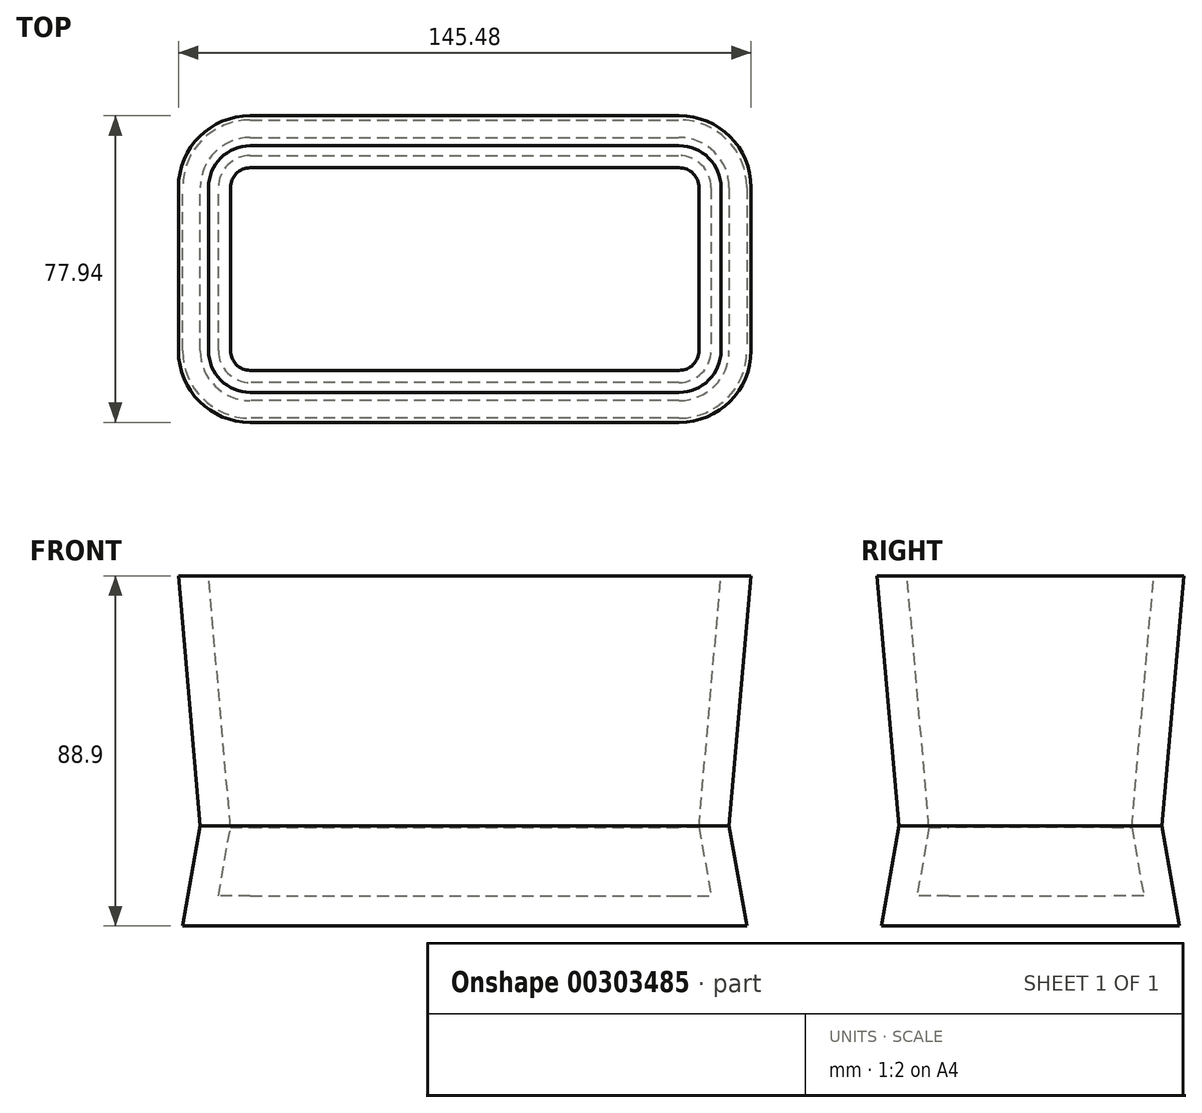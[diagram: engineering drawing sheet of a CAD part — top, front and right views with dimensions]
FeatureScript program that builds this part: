
annotation { "Feature Type Name" : "Feature", "Feature Type Description" : "" }
export const myFeature = defineFeature(function(context is Context, id is Id, definition is map)
    precondition{}
    {
        {
            var Q0;
            Q0=qCreatedBy(makeId("Top.planeOp"),FACE);
            var sketch = newSketch(context, id + "F0", { "sketchPlane" : qUnion([Q0])});
            skLineSegment(sketch, "E0.bottom", {"start": v(-54.48, 33.42) * mm, "end": v(54.48, 33.42) * mm});
            skLineSegment(sketch, "E0.top", {"start": v(-54.48, -33.42) * mm, "end": v(54.48, -33.42) * mm});
            skLineSegment(sketch, "E0.left", {"start": v(-67.18, 20.72) * mm, "end": v(-67.18, -20.72) * mm});
            skLineSegment(sketch, "E0.right", {"start": v(67.18, 20.72) * mm, "end": v(67.18, -20.72) * mm});
            skPoint(sketch, "E0.middle", {"position": v(0, 0) * mm});
            skPoint(sketch, "E1.visualSharp", {"position": v(-67.18, 33.42) * mm});
            skArc(sketch, "E1.filletArc", {"start": v(-54.48, 33.42) * mm, "mid": v(-63.47, 29.7) * mm, "end": v(-67.18, 20.72) * mm});
            skPoint(sketch, "E2.visualSharp", {"position": v(67.18, 33.42) * mm});
            skArc(sketch, "E2.filletArc", {"start": v(67.18, 20.72) * mm, "mid": v(63.47, 29.7) * mm, "end": v(54.48, 33.42) * mm});
            skPoint(sketch, "E3.visualSharp", {"position": v(-67.18, -33.42) * mm});
            skArc(sketch, "E3.filletArc", {"start": v(-67.18, -20.72) * mm, "mid": v(-63.47, -29.7) * mm, "end": v(-54.48, -33.42) * mm});
            skPoint(sketch, "E4.visualSharp", {"position": v(67.18, -33.42) * mm});
            skArc(sketch, "E4.filletArc", {"start": v(54.48, -33.42) * mm, "mid": v(63.47, -29.7) * mm, "end": v(67.18, -20.72) * mm});
            skSolve(sketch);
        }
        {
            var Q0;
            Q0=makeQuery(id+"F0.imprint","IMPRINT",FACE,{"disambiguationData":[TD([[makeQuery(id+"F0.imprint","IMPRINT",EDGE,{"derivedFrom":sQuery(id+"F0.wireOp",EDGE,"E0.bottom")}),-1.0]])]});
            extrude(context, id + "F1", {"entities" : qUnion([Q0]), "depth" : 63.5 * mm, "hasDraft" : true, "draftAngle" : 5 * degree, "hasSecondDirection" : true, "secondDirectionOppositeDirection" : true, "secondDirectionDepth" : 25.4 * mm, "hasSecondDirectionDraft" : true, "secondDirectionDraftAngle" : 10 * degree});
        }
        {
            var Q0;
            Q0=makeQuery(id+"F1.opExtrude","CAP_FACE",FACE,{"disambiguationData":[OSD([sQuery(id+"F0.wireOp",EDGE,"E0.bottom"),sQuery(id+"F0.wireOp",EDGE,"E0.top"),sQuery(id+"F0.wireOp",EDGE,"E0.left"),sQuery(id+"F0.wireOp",EDGE,"E0.right"),sQuery(id+"F0.wireOp",EDGE,"E1.filletArc"),sQuery(id+"F0.wireOp",EDGE,"E2.filletArc"),sQuery(id+"F0.wireOp",EDGE,"E3.filletArc"),sQuery(id+"F0.wireOp",EDGE,"E4.filletArc")])],"isStart":false});
            shell(context, id + "F2", {"entities" : qUnion([Q0]), "thickness" : 7.62 * mm});
        }
    });
